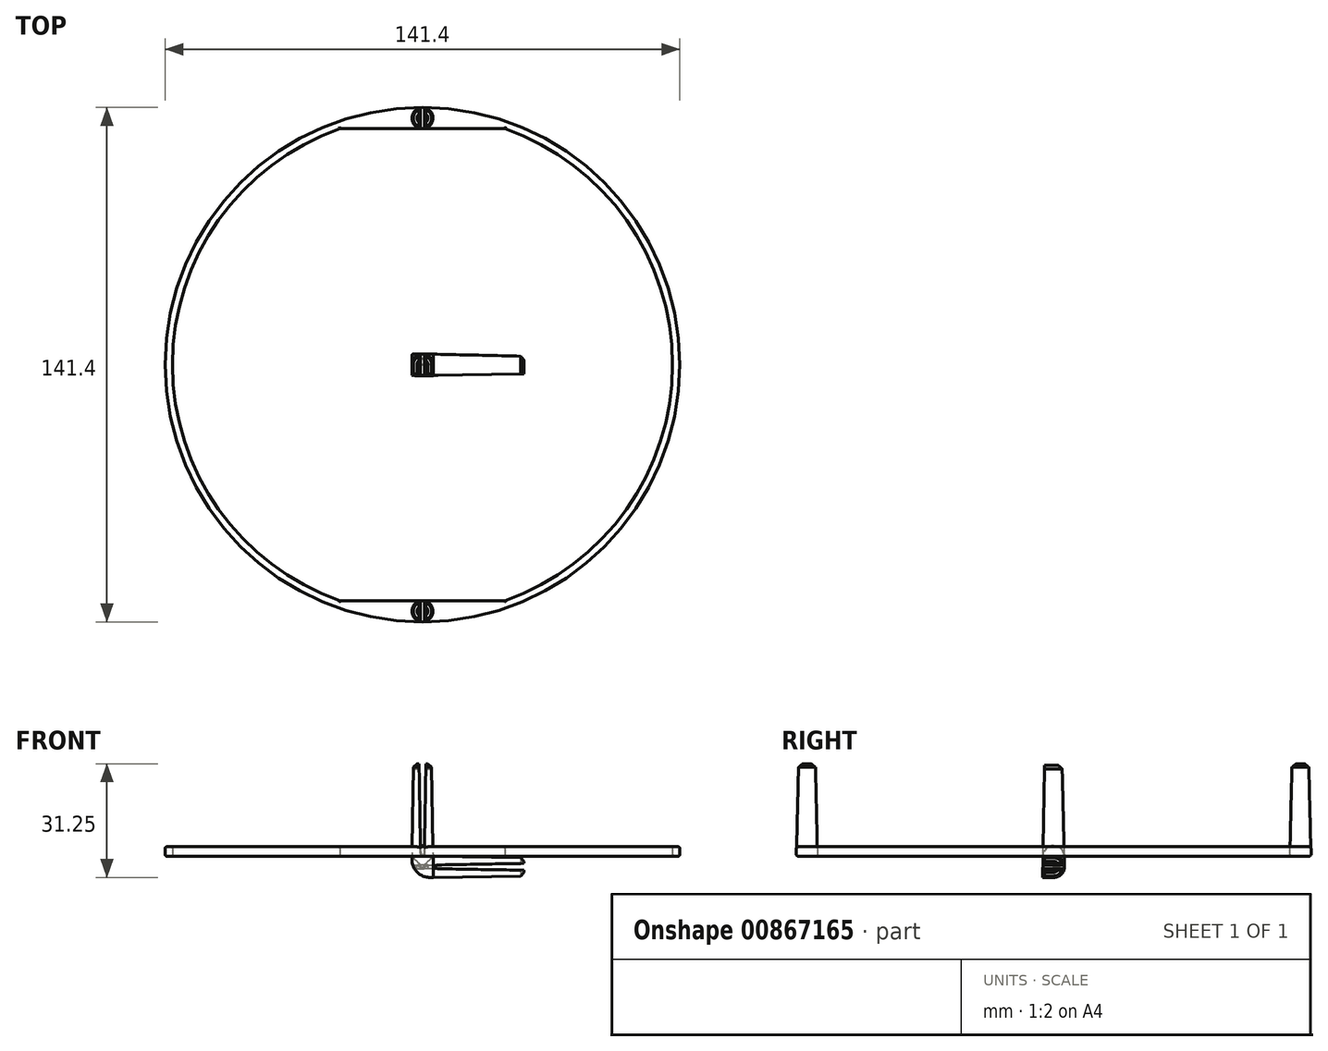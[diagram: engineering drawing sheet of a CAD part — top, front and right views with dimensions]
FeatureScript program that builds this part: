
annotation { "Feature Type Name" : "Feature", "Feature Type Description" : "" }
export const myFeature = defineFeature(function(context is Context, id is Id, definition is map)
    precondition{}
    {
        {
            assignVariable(context, id + "F0", {"name" : "discHeight", "anyValue" : 2.58});
        }
        {
            var Q0;
            Q0=qCreatedBy(makeId("Top.planeOp"),FACE);
            var sketch = newSketch(context, id + "F1", { "sketchPlane" : qUnion([Q0])});
            skCircle(sketch, "E0", {"center": v(0, 0) * mm, "radius": 70.7 * mm});
            skCircle(sketch, "E1", {"center": v(0, 0) * mm, "radius": 68.7 * mm});
            skLineSegment(sketch, "E2", {"start": v(0, -64.84) * mm, "end": v(0, -70.7) * mm, "construction": true});
            skLineSegment(sketch, "E3", {"start": v(0, -70.7) * mm, "end": v(0, -67.77) * mm, "construction": true});
            skCircle(sketch, "E4", {"center": v(0, -67.77) * mm, "radius": 2.92 * mm});
            skLineSegment(sketch, "E5", {"start": v(0, 0) * mm, "end": v(-70.7, 0) * mm, "construction": true});
            skLineSegment(sketch, "E6", {"start": v(0, -64.84) * mm, "end": v(22.67, -64.84) * mm});
            skLineSegment(sketch, "E7.MirrorCS", {"start": v(0, -64.84) * mm, "end": v(-22.67, -64.84) * mm});
            skLineSegment(sketch, "E8.MirrorCS", {"start": v(0, 64.84) * mm, "end": v(-22.67, 64.84) * mm});
            skLineSegment(sketch, "E9.MirrorCS", {"start": v(0, 64.84) * mm, "end": v(22.67, 64.84) * mm});
            skLineSegment(sketch, "E10.0", {"start": v(0.5, -70.7) * mm, "end": v(0.5, -67.77) * mm});
            skLineSegment(sketch, "E11.MirrorCS", {"start": v(-0.5, -70.7) * mm, "end": v(-0.5, -67.77) * mm});
            skLineSegment(sketch, "E12", {"start": v(0, -67.77) * mm, "end": v(-2.92, -67.77) * mm, "construction": true});
            skLineSegment(sketch, "E13.MirrorCS", {"start": v(-0.5, -64.84) * mm, "end": v(-0.5, -67.77) * mm});
            skLineSegment(sketch, "E14.MirrorCS", {"start": v(0.5, -64.84) * mm, "end": v(0.5, -67.77) * mm});
            skSolve(sketch);
        }
        {
            var Q0;
            {var subQ0=sQuery(id+"F1.wireOp",EDGE,"E0");Q0=makeQuery(id+"F1.imprint","IMPRINT",FACE,{"disambiguationData":[TD([[makeQuery(id+"F1.imprint","IMPRINT",EDGE,{"derivedFrom":subQ0}),1.0]])]});}
            var Q1;
            {var subQ0=sQuery(id+"F1.wireOp",EDGE,"E4");var subQ1=sQuery(id+"F1.wireOp",EDGE,"E1");var subQ2=makeQuery(id+"F1.imprint","INTERSECT",VERTEX,{"disambiguationData":[OD(0.0)],"derivedFrom":[subQ1,subQ0]});Q1=makeQuery(id+"F1.imprint","IMPRINT",FACE,{"disambiguationData":[TD([[makeQuery(id+"F1.imprint","IMPRINT",EDGE,{"disambiguationData":[TD([[subQ2,-1.0]])],"derivedFrom":subQ1}),-1.0]])]});}
            var Q2;
            {var subQ0=sQuery(id+"F1.wireOp",EDGE,"E7.MirrorCS");Q2=makeQuery(id+"F1.imprint","IMPRINT",FACE,{"disambiguationData":[TD([[makeQuery(id+"F1.imprint","IMPRINT",EDGE,{"derivedFrom":subQ0}),1.0]])]});}
            var Q3;
            {var subQ0=sQuery(id+"F1.wireOp",EDGE,"E6");Q3=makeQuery(id+"F1.imprint","IMPRINT",FACE,{"disambiguationData":[TD([[makeQuery(id+"F1.imprint","IMPRINT",EDGE,{"derivedFrom":subQ0}),-1.0]])]});}
            var Q4;
            {var subQ0=sQuery(id+"F1.wireOp",EDGE,"E8.MirrorCS");Q4=makeQuery(id+"F1.imprint","IMPRINT",FACE,{"disambiguationData":[TD([[makeQuery(id+"F1.imprint","IMPRINT",EDGE,{"derivedFrom":subQ0}),-1.0]])]});}
            var Q5;
            {var subQ0=sQuery(id+"F1.wireOp",EDGE,"E4");var subQ1=sQuery(id+"F1.wireOp",EDGE,"E1");var subQ2=makeQuery(id+"F1.imprint","INTERSECT",VERTEX,{"disambiguationData":[OD(0.0)],"derivedFrom":[subQ1,subQ0]});Q5=makeQuery(id+"F1.imprint","IMPRINT",FACE,{"disambiguationData":[TD([[makeQuery(id+"F1.imprint","IMPRINT",EDGE,{"disambiguationData":[TD([[subQ2,-1.0]])],"derivedFrom":subQ1}),1.0]])]});}
            var Q6;
            {var subQ0=sQuery(id+"F1.wireOp",EDGE,"E6");var subQ1=sQuery(id+"F1.wireOp",EDGE,"E1");var subQ2=makeQuery(id+"F1.imprint","INTERSECT",VERTEX,{"derivedFrom":[subQ1,subQ0]});Q6=makeQuery(id+"F1.imprint","IMPRINT",FACE,{"disambiguationData":[TD([[makeQuery(id+"F1.imprint","IMPRINT",EDGE,{"disambiguationData":[TD([[subQ2,1.0]])],"derivedFrom":subQ1}),1.0]])]});}
            var Q7;
            {var subQ0=sQuery(id+"F1.wireOp",EDGE,"E7.MirrorCS");var subQ1=sQuery(id+"F1.wireOp",EDGE,"E1");var subQ2=makeQuery(id+"F1.imprint","INTERSECT",VERTEX,{"derivedFrom":[subQ1,subQ0]});Q7=makeQuery(id+"F1.imprint","IMPRINT",FACE,{"disambiguationData":[TD([[makeQuery(id+"F1.imprint","IMPRINT",EDGE,{"disambiguationData":[TD([[subQ2,-1.0]])],"derivedFrom":subQ1}),1.0]])]});}
            var Q8;
            {var subQ0=sQuery(id+"F1.wireOp",EDGE,"E10.0");var subQ1=sQuery(id+"F1.wireOp",EDGE,"E1");var subQ2=makeQuery(id+"F1.imprint","INTERSECT",VERTEX,{"derivedFrom":[subQ1,subQ0]});Q8=makeQuery(id+"F1.imprint","IMPRINT",FACE,{"disambiguationData":[TD([[makeQuery(id+"F1.imprint","IMPRINT",EDGE,{"disambiguationData":[TD([[subQ2,-1.0]])],"derivedFrom":subQ1}),1.0]])]});}
            var Q9;
            {var subQ0=sQuery(id+"F1.wireOp",EDGE,"E10.0");var subQ1=sQuery(id+"F1.wireOp",EDGE,"E1");var subQ2=makeQuery(id+"F1.imprint","INTERSECT",VERTEX,{"derivedFrom":[subQ1,subQ0]});Q9=makeQuery(id+"F1.imprint","IMPRINT",FACE,{"disambiguationData":[TD([[makeQuery(id+"F1.imprint","IMPRINT",EDGE,{"disambiguationData":[TD([[subQ2,-1.0]])],"derivedFrom":subQ1}),-1.0]])]});}
            var Q10;
            {var subQ1=sQuery(id+"F1.wireOp",EDGE,"E1");var subQ6=sQuery(id+"F1.wireOp",EDGE,"E11.MirrorCS");var subQ8=makeQuery(id+"F1.imprint","INTERSECT",VERTEX,{"derivedFrom":[subQ1,subQ6]});Q10=makeQuery(id+"F1.imprint","IMPRINT",FACE,{"disambiguationData":[TD([[makeQuery(id+"F1.imprint","IMPRINT",EDGE,{"disambiguationData":[TD([[subQ8,-1.0]])],"derivedFrom":subQ1}),-1.0]])]});}
            var Q11;
            {var subQ6=sQuery(id+"F1.wireOp",EDGE,"E1");var subQ10=sQuery(id+"F1.wireOp",EDGE,"E11.MirrorCS");var subQ11=makeQuery(id+"F1.imprint","INTERSECT",VERTEX,{"derivedFrom":[subQ6,subQ10]});Q11=makeQuery(id+"F1.imprint","IMPRINT",FACE,{"disambiguationData":[TD([[makeQuery(id+"F1.imprint","IMPRINT",EDGE,{"disambiguationData":[TD([[subQ11,-1.0]])],"derivedFrom":subQ6}),1.0]])]});}
            var Q12;
            {var subQ6=sQuery(id+"F1.wireOp",EDGE,"E11.MirrorCS");var subQ9=sQuery(id+"F1.wireOp",EDGE,"E0");var subQ12=makeQuery(id+"F1.imprint","INTERSECT",VERTEX,{"derivedFrom":[subQ9,subQ6]});Q12=makeQuery(id+"F1.imprint","IMPRINT",FACE,{"disambiguationData":[TD([[makeQuery(id+"F1.imprint","IMPRINT",EDGE,{"disambiguationData":[TD([[subQ12,1.0]])],"derivedFrom":subQ9}),1.0]])]});}
            extrude(context, id + "F2", {"entities" : qUnion([Q0, Q1, Q2, Q3, Q4, Q5, Q6, Q7, Q8, Q9, Q10, Q11, Q12]), "depth" : (getVariable(context, 'discHeight')) * mm, "offsetDistance" : 25 * mm});
        }
        {
            assignVariable(context, id + "F3", {"name" : "mountHeight", "anyValue" : 25.4});
        }
        {
            var Q0;
            {var subQ0=sQuery(id+"F1.wireOp",EDGE,"E4");var subQ1=sQuery(id+"F1.wireOp",EDGE,"E1");var subQ2=makeQuery(id+"F1.imprint","INTERSECT",VERTEX,{"disambiguationData":[OD(0.0)],"derivedFrom":[subQ1,subQ0]});Q0=makeQuery(id+"F1.imprint","IMPRINT",FACE,{"disambiguationData":[TD([[makeQuery(id+"F1.imprint","IMPRINT",EDGE,{"disambiguationData":[TD([[subQ2,-1.0]])],"derivedFrom":subQ1}),1.0]])]});}
            var Q1;
            {var subQ0=sQuery(id+"F1.wireOp",EDGE,"E4");var subQ1=sQuery(id+"F1.wireOp",EDGE,"E1");var subQ2=makeQuery(id+"F1.imprint","INTERSECT",VERTEX,{"disambiguationData":[OD(0.0)],"derivedFrom":[subQ1,subQ0]});Q1=makeQuery(id+"F1.imprint","IMPRINT",FACE,{"disambiguationData":[TD([[makeQuery(id+"F1.imprint","IMPRINT",EDGE,{"disambiguationData":[TD([[subQ2,-1.0]])],"derivedFrom":subQ1}),-1.0]])]});}
            var Q2;
            {var subQ0=sQuery(id+"F1.wireOp",EDGE,"E10.0");var subQ1=sQuery(id+"F1.wireOp",EDGE,"E1");var subQ2=makeQuery(id+"F1.imprint","INTERSECT",VERTEX,{"derivedFrom":[subQ1,subQ0]});Q2=makeQuery(id+"F1.imprint","IMPRINT",FACE,{"disambiguationData":[TD([[makeQuery(id+"F1.imprint","IMPRINT",EDGE,{"disambiguationData":[TD([[subQ2,-1.0]])],"derivedFrom":subQ1}),1.0]])]});}
            var Q3;
            {var subQ0=sQuery(id+"F1.wireOp",EDGE,"E10.0");var subQ1=sQuery(id+"F1.wireOp",EDGE,"E1");var subQ2=makeQuery(id+"F1.imprint","INTERSECT",VERTEX,{"derivedFrom":[subQ1,subQ0]});Q3=makeQuery(id+"F1.imprint","IMPRINT",FACE,{"disambiguationData":[TD([[makeQuery(id+"F1.imprint","IMPRINT",EDGE,{"disambiguationData":[TD([[subQ2,-1.0]])],"derivedFrom":subQ1}),-1.0]])]});}
            extrude(context, id + "F4", {"entities" : qUnion([Q0, Q1, Q2, Q3]), "depth" : (getVariable(context, 'mountHeight')) * mm, "offsetDistance" : 25 * mm, "hasDraft" : true, "draftAngle" : 1 * degree, "draftPullDirection" : true});
        }
        {
            var Q0;
            Q0=makeQuery(id+"F4.opExtrude","SWEPT_BODY",BODY,{"disambiguationData":[OSD([sQuery(id+"F1.wireOp",EDGE,"E4")])]});
            var Q1;
            Q1=qCreatedBy(makeId("Front.planeOp"),FACE);
            mirror(context, id + "F5", {"operationType" : NewBodyOperationType.ADD, "entities" : qUnion([Q0]), "mirrorPlane" : qUnion([Q1])});
        }
        {
            var Q0;
            Q0=makeQuery(id+"F5.opPattern","COPY",EDGE,{"derivedFrom":makeQuery(id+"F4.opExtrude","CAP_EDGE",EDGE,{"disambiguationData":[OSD([sQuery(id+"F1.wireOp",EDGE,"E4")])],"isStart":false}),"instanceName":"1"});
            var Q1;
            Q1=makeQuery(id+"F4.opExtrude","CAP_EDGE",EDGE,{"disambiguationData":[OSD([sQuery(id+"F1.wireOp",EDGE,"E4")])],"isStart":false});
            chamfer(context, id + "F6", {"entities" : qUnion([Q0, Q1]), "width" : 1 * mm, "tangentPropagation" : true});
        }
        {
            var Q0;
            Q0=makeQuery(id+"F5.boolean.opBoolean","SPLIT",EDGE,{"disambiguationData":[OD(0.0)],"derivedFrom":makeQuery(id+"F2.opExtrude","CAP_EDGE",EDGE,{"disambiguationData":[OSD([sQuery(id+"F1.wireOp",EDGE,"E1")])],"isStart":false})});
            var Q1;
            Q1=makeQuery(id+"F2.opExtrude","CAP_EDGE",EDGE,{"disambiguationData":[OSD([sQuery(id+"F1.wireOp",EDGE,"E0")])],"isStart":false});
            var Q2;
            Q2=makeQuery(id+"F5.boolean.opBoolean","SPLIT",EDGE,{"disambiguationData":[OD(1.0)],"derivedFrom":makeQuery(id+"F2.opExtrude","CAP_EDGE",EDGE,{"disambiguationData":[OSD([sQuery(id+"F1.wireOp",EDGE,"E1")])],"isStart":true})});
            var Q3;
            Q3=makeQuery(id+"F2.opExtrude","CAP_EDGE",EDGE,{"disambiguationData":[OSD([sQuery(id+"F1.wireOp",EDGE,"E0")])],"isStart":true});
            var Q4;
            Q4=makeQuery(id+"F5.opPattern","COPY",EDGE,{"derivedFrom":makeQuery(id+"F4.opExtrude","CAP_EDGE",EDGE,{"disambiguationData":[OSD([sQuery(id+"F1.wireOp",EDGE,"E4")])],"isStart":true}),"instanceName":"1"});
            var Q5;
            Q5=makeQuery(id+"F5.boolean.opBoolean","SPLIT",EDGE,{"disambiguationData":[OD(1.0)],"derivedFrom":makeQuery(id+"F2.opExtrude","CAP_EDGE",EDGE,{"disambiguationData":[OSD([sQuery(id+"F1.wireOp",EDGE,"E1")])],"isStart":false})});
            var Q6;
            Q6=makeQuery(id+"F4.opExtrude","CAP_EDGE",EDGE,{"disambiguationData":[OSD([sQuery(id+"F1.wireOp",EDGE,"E4")])],"isStart":true});
            var Q7;
            Q7=makeQuery(id+"F5.boolean.opBoolean","SPLIT",EDGE,{"disambiguationData":[OD(0.0)],"derivedFrom":makeQuery(id+"F2.opExtrude","CAP_EDGE",EDGE,{"disambiguationData":[OSD([sQuery(id+"F1.wireOp",EDGE,"E1")])],"isStart":true})});
            var Q8;
            Q8=makeQuery(id+"F2.opExtrude","CAP_EDGE",EDGE,{"disambiguationData":[OSD([sQuery(id+"F1.wireOp",EDGE,"E6"),sQuery(id+"F1.wireOp",EDGE,"E7.MirrorCS")])],"isStart":false});
            var Q9;
            Q9=makeQuery(id+"F2.opExtrude","CAP_EDGE",EDGE,{"disambiguationData":[OSD([sQuery(id+"F1.wireOp",EDGE,"E6"),sQuery(id+"F1.wireOp",EDGE,"E7.MirrorCS")])],"isStart":true});
            var Q10;
            Q10=makeQuery(id+"F2.opExtrude","CAP_EDGE",EDGE,{"disambiguationData":[OSD([sQuery(id+"F1.wireOp",EDGE,"E8.MirrorCS"),sQuery(id+"F1.wireOp",EDGE,"E9.MirrorCS")])],"isStart":false});
            var Q11;
            Q11=makeQuery(id+"F2.opExtrude","CAP_EDGE",EDGE,{"disambiguationData":[OSD([sQuery(id+"F1.wireOp",EDGE,"E8.MirrorCS"),sQuery(id+"F1.wireOp",EDGE,"E9.MirrorCS")])],"isStart":true});
            fillet(context, id + "F7", {"entities" : qUnion([Q0, Q1, Q2, Q3, Q4, Q5, Q6, Q7, Q8, Q9, Q10, Q11]), "radius" : 0.5 * mm, "tangentPropagation" : true, "allowEdgeOverflow" : false});
        }
        {
            var Q0;
            Q0=qCreatedBy(makeId("Top.planeOp"),FACE);
            var sketch = newSketch(context, id + "F8", { "sketchPlane" : qUnion([Q0])});
            skCircle(sketch, "E15", {"center": v(0, 0) * mm, "radius": 2.93 * mm});
            skLineSegment(sketch, "E16", {"start": v(0, 2.93) * mm, "end": v(0, -2.93) * mm});
            skLineSegment(sketch, "E17.0", {"start": v(0.5, 2.88) * mm, "end": v(0.5, -2.88) * mm});
            skLineSegment(sketch, "E18.MirrorCS", {"start": v(-0.5, 2.88) * mm, "end": v(-0.5, -2.88) * mm});
            skPoint(sketch, "E19.orphan", {"position": v(0.5, 2.92) * mm});
            skPoint(sketch, "E20.orphan", {"position": v(-0.5, 2.92) * mm});
            skPoint(sketch, "E21.orphan", {"position": v(0.5, -2.93) * mm});
            skPoint(sketch, "E22.orphan", {"position": v(-0.5, -2.93) * mm});
            skLineSegment(sketch, "E23.top", {"start": v(-2.93, -2.93) * mm, "end": v(2.93, -2.93) * mm});
            skLineSegment(sketch, "E23.left", {"start": v(-2.93, 0) * mm, "end": v(-2.93, -2.93) * mm});
            skLineSegment(sketch, "E23.right", {"start": v(2.93, 0) * mm, "end": v(2.93, -2.93) * mm});
            skSolve(sketch);
        }
        {
            var Q0;
            {var subQ0=sQuery(id+"F8.wireOp",EDGE,"E16");Q0=makeQuery(id+"F8.imprint","IMPRINT",FACE,{"disambiguationData":[TD([[makeQuery(id+"F8.imprint","IMPRINT",EDGE,{"derivedFrom":subQ0}),1.0]])]});}
            var Q1;
            {var subQ0=sQuery(id+"F8.wireOp",EDGE,"E17.0");Q1=makeQuery(id+"F8.imprint","IMPRINT",FACE,{"disambiguationData":[TD([[makeQuery(id+"F8.imprint","IMPRINT",EDGE,{"derivedFrom":subQ0}),1.0]])]});}
            var Q2;
            Q2=sQuery(id+"F8.wireOp",EDGE,"E16");
            revolve(context, id + "F9", {"surfaceOperationType" : NewSurfaceOperationType.NEW, "entities" : qUnion([Q0, Q1]), "axis" : qUnion([Q2]), "revolveType" : RevolveType.FULL});
        }
        {
            var Q0;
            {var subQ0=sQuery(id+"F8.wireOp",EDGE,"E17.0");Q0=makeQuery(id+"F8.imprint","IMPRINT",FACE,{"disambiguationData":[TD([[makeQuery(id+"F8.imprint","IMPRINT",EDGE,{"derivedFrom":subQ0}),1.0]])]});}
            var Q1;
            {var subQ0=sQuery(id+"F8.wireOp",EDGE,"E18.MirrorCS");Q1=makeQuery(id+"F8.imprint","IMPRINT",FACE,{"disambiguationData":[TD([[makeQuery(id+"F8.imprint","IMPRINT",EDGE,{"derivedFrom":subQ0}),-1.0]])]});}
            var Q2;
            {var subQ2=sQuery(id+"F8.wireOp",EDGE,"E23.left");Q2=makeQuery(id+"F8.imprint","IMPRINT",FACE,{"disambiguationData":[TD([[makeQuery(id+"F8.imprint","IMPRINT",EDGE,{"derivedFrom":subQ2}),1.0]])]});}
            var Q3;
            {var subQ4=sQuery(id+"F8.wireOp",EDGE,"E23.right");Q3=makeQuery(id+"F8.imprint","IMPRINT",FACE,{"disambiguationData":[TD([[makeQuery(id+"F8.imprint","IMPRINT",EDGE,{"derivedFrom":subQ4}),-1.0]])]});}
            extrude(context, id + "F10", {"entities" : qUnion([Q0, Q1, Q2, Q3]), "depth" : 25 * mm, "offsetDistance" : 25 * mm, "hasDraft" : true, "draftAngle" : 1 * degree, "draftPullDirection" : true});
        }
        {
            var Q0;
            {var subQ0=sQuery(id+"F8.wireOp",EDGE,"E18.MirrorCS");var subQ1=sQuery(id+"F8.wireOp",EDGE,"E15");Q0=makeQuery(id+"F10.opExtrude","CAP_EDGE",EDGE,{"disambiguationData":[OSD([subQ1]),TDD([makeQuery(id+"F8.imprint","IMPRINT",EDGE,{"disambiguationData":[TD([[makeQuery(id+"F8.imprint","INTERSECT",VERTEX,{"disambiguationData":[OD(0.0)],"derivedFrom":[subQ1,subQ0]}),-1.0]])],"derivedFrom":subQ1})])],"isStart":false});}
            var Q1;
            {var subQ0=sQuery(id+"F8.wireOp",EDGE,"E17.0");var subQ1=sQuery(id+"F8.wireOp",EDGE,"E15");Q1=makeQuery(id+"F10.opExtrude","CAP_EDGE",EDGE,{"disambiguationData":[OSD([subQ1]),TDD([makeQuery(id+"F8.imprint","IMPRINT",EDGE,{"disambiguationData":[TD([[makeQuery(id+"F8.imprint","INTERSECT",VERTEX,{"disambiguationData":[OD(0.0)],"derivedFrom":[subQ1,subQ0]}),1.0]])],"derivedFrom":subQ1})])],"isStart":false});}
            chamfer(context, id + "F11", {"entities" : qUnion([Q0, Q1]), "width" : 1 * mm, "tangentPropagation" : true});
        }
        {
            var Q0;
            Q0=makeQuery(id+"F10.opExtrude","SWEPT_BODY",BODY,{"disambiguationData":[OSD([sQuery(id+"F8.wireOp",EDGE,"E15"),sQuery(id+"F8.wireOp",EDGE,"E18.MirrorCS")])]});
            var Q1;
            Q1=makeQuery(id+"F10.opExtrude","SWEPT_BODY",BODY,{"disambiguationData":[OSD([sQuery(id+"F8.wireOp",EDGE,"E15"),sQuery(id+"F8.wireOp",EDGE,"E17.0")])]});
            var Q2;
            Q2=sQuery(id+"F8.wireOp",EDGE,"E23.left");
            transform(context, id + "F12", {"entities" : qUnion([Q0, Q1]), "transformType" : TransformType.ROTATION, "transformAxis" : qUnion([Q2]), "angle" : 90 * degree, "oppositeDirection" : true, "makeCopy" : true});
        }
        {
            var Q0;
            Q0=makeQuery(id+"F12.opPattern","COPY",BODY,{"derivedFrom":makeQuery(id+"F10.opExtrude","SWEPT_BODY",BODY,{"disambiguationData":[OSD([sQuery(id+"F8.wireOp",EDGE,"E15"),sQuery(id+"F8.wireOp",EDGE,"E18.MirrorCS"),sQuery(id+"F8.wireOp",EDGE,"E23.top"),sQuery(id+"F8.wireOp",EDGE,"E23.left")])]}),"instanceName":"1"});
            var Q1;
            Q1=makeQuery(id+"F12.opPattern","COPY",BODY,{"derivedFrom":makeQuery(id+"F10.opExtrude","SWEPT_BODY",BODY,{"disambiguationData":[OSD([sQuery(id+"F8.wireOp",EDGE,"E15"),sQuery(id+"F8.wireOp",EDGE,"E17.0"),sQuery(id+"F8.wireOp",EDGE,"E23.top"),sQuery(id+"F8.wireOp",EDGE,"E23.right")])]}),"instanceName":"1"});
            var Q2;
            Q2=sQuery(id+"F8.wireOp",EDGE,"E23.top");
            transform(context, id + "F13", {"entities" : qUnion([Q0, Q1]), "transformType" : TransformType.TRANSLATION_ENTITY, "oppositeDirectionEntity" : false, "transformLine" : qUnion([Q2]), "makeCopy" : false});
        }
        {
            var Q0;
            Q0=qCreatedBy(makeId("Front.planeOp"),FACE);
            var sketch = newSketch(context, id + "F14", { "sketchPlane" : qUnion([Q0])});
            skPoint(sketch, "E24.0", {"position": v(2.93, -5.85) * mm});
            skPoint(sketch, "E25.0", {"position": v(-2.93, 0) * mm});
            skLineSegment(sketch, "E26.0", {"start": v(2.93, 0) * mm, "end": v(2.93, -2.93) * mm});
            skLineSegment(sketch, "E26.1", {"start": v(2.93, -2.93) * mm, "end": v(2.93, -5.85) * mm});
            skLineSegment(sketch, "E26.2", {"start": v(-2.93, 0) * mm, "end": v(2.93, 0) * mm});
            skLineSegment(sketch, "E27.bottom", {"start": v(2.93, -5.85) * mm, "end": v(-2.93, -5.85) * mm});
            skLineSegment(sketch, "E27.top", {"start": v(2.93, 0) * mm, "end": v(-2.93, 0) * mm});
            skLineSegment(sketch, "E27.left", {"start": v(2.93, -5.85) * mm, "end": v(2.93, 0) * mm});
            skLineSegment(sketch, "E27.right", {"start": v(-2.93, -5.85) * mm, "end": v(-2.93, 0) * mm});
            skSolve(sketch);
        }
        {
            var Q0;
            Q0 = qSketchRegion(id + "F14", true);
            var Q1;
            {var subQ0=sQuery(id+"F8.wireOp",EDGE,"E23.top");Q1=makeQuery(id+"F10.opExtrude","SWEPT_FACE",FACE,{"disambiguationData":[OSD([subQ0]),TDD([makeQuery(id+"F8.imprint","IMPRINT",EDGE,{"disambiguationData":[TD([[makeQuery(id+"F8.imprint","INTERSECT",VERTEX,{"derivedFrom":[subQ0,sQuery(id+"F8.wireOp",EDGE,"E23.left")]}),-1.0]])],"derivedFrom":subQ0})])]});}
            extrude(context, id + "F15", {"entities" : qUnion([Q0]), "endBound" : BoundingType.UP_TO_SURFACE, "depth" : 25 * mm, "endBoundEntityFace" : qUnion([Q1]), "offsetDistance" : 25 * mm});
        }
        {
            var Q0;
            Q0=makeQuery(id+"F12.opPattern","COPY",FACE,{"derivedFrom":makeQuery(id+"F10.opExtrude","CAP_FACE",FACE,{"disambiguationData":[OSD([sQuery(id+"F8.wireOp",EDGE,"E15"),sQuery(id+"F8.wireOp",EDGE,"E17.0"),sQuery(id+"F8.wireOp",EDGE,"E23.top"),sQuery(id+"F8.wireOp",EDGE,"E23.right")])],"isStart":true}),"instanceName":"1"});
            var Q1;
            Q1=makeQuery(id+"F12.opPattern","COPY",FACE,{"derivedFrom":makeQuery(id+"F10.opExtrude","CAP_FACE",FACE,{"disambiguationData":[OSD([sQuery(id+"F8.wireOp",EDGE,"E15"),sQuery(id+"F8.wireOp",EDGE,"E18.MirrorCS"),sQuery(id+"F8.wireOp",EDGE,"E23.top"),sQuery(id+"F8.wireOp",EDGE,"E23.left")])],"isStart":true}),"instanceName":"1"});
            var Q2;
            Q2=makeQuery(id+"F15.opExtrude","SWEPT_FACE",FACE,{"disambiguationData":[OSD([sQuery(id+"F14.wireOp",EDGE,"E27.right")])]});
            extrude(context, id + "F16", {"entities" : qUnion([Q0, Q1]), "operationType" : NewBodyOperationType.ADD, "endBound" : BoundingType.UP_TO_SURFACE, "depth" : 25 * mm, "endBoundEntityFace" : qUnion([Q2]), "offsetDistance" : 25 * mm});
        }
        {
            var Q0;
            {var subQ0=sQuery(id+"F8.wireOp",EDGE,"E18.MirrorCS");Q0=makeQuery(id+"F8.imprint","IMPRINT",FACE,{"disambiguationData":[TD([[makeQuery(id+"F8.imprint","IMPRINT",EDGE,{"derivedFrom":subQ0}),-1.0]])]});}
            var Q1;
            {var subQ0=sQuery(id+"F8.wireOp",EDGE,"E17.0");Q1=makeQuery(id+"F8.imprint","IMPRINT",FACE,{"disambiguationData":[TD([[makeQuery(id+"F8.imprint","IMPRINT",EDGE,{"derivedFrom":subQ0}),1.0]])]});}
            var Q2;
            Q2=makeQuery(id+"F16.opExtrude","SWEPT_FACE",FACE,{"disambiguationData":[OSD([sQuery(id+"F8.wireOp",EDGE,"E18.MirrorCS")])]});
            extrude(context, id + "F17", {"entities" : qUnion([Q0, Q1]), "operationType" : NewBodyOperationType.ADD, "endBound" : BoundingType.UP_TO_SURFACE, "oppositeDirection" : true, "depth" : 25 * mm, "endBoundEntityFace" : qUnion([Q2]), "offsetDistance" : 25 * mm});
        }
        {
            var Q0;
            {var subQ0=sQuery(id+"F8.wireOp",EDGE,"E16");Q0=makeQuery(id+"F8.imprint","IMPRINT",FACE,{"disambiguationData":[TD([[makeQuery(id+"F8.imprint","IMPRINT",EDGE,{"derivedFrom":subQ0}),1.0]])]});}
            var Q1;
            {var subQ0=sQuery(id+"F8.wireOp",EDGE,"E16");Q1=makeQuery(id+"F8.imprint","IMPRINT",FACE,{"disambiguationData":[TD([[makeQuery(id+"F8.imprint","IMPRINT",EDGE,{"derivedFrom":subQ0}),-1.0]])]});}
            var Q2;
            Q2=makeQuery(id+"F16.opExtrude","SWEPT_FACE",FACE,{"disambiguationData":[OSD([sQuery(id+"F8.wireOp",EDGE,"E18.MirrorCS")])]});
            extrude(context, id + "F18", {"entities" : qUnion([Q0, Q1]), "operationType" : NewBodyOperationType.ADD, "endBound" : BoundingType.UP_TO_SURFACE, "oppositeDirection" : true, "depth" : 25 * mm, "endBoundEntityFace" : qUnion([Q2]), "offsetDistance" : 25 * mm});
        }
        {
            var Q0;
            {var subQ0=sQuery(id+"F8.wireOp",EDGE,"E18.MirrorCS");Q0=makeQuery(id+"F18.boolean.opBoolean","MERGE",FACE,{"derivedFrom":[makeQuery(id+"F16.opExtrude","SWEPT_FACE",FACE,{"disambiguationData":[OSD([subQ0])]}),makeQuery(id+"F18.opExtrude","CAP_FACE",FACE,{"disambiguationData":[OSD([subQ0])],"isStart":false})]});}
            var Q1;
            Q1=makeQuery(id+"F16.opExtrude","SWEPT_FACE",FACE,{"disambiguationData":[OSD([sQuery(id+"F8.wireOp",EDGE,"E17.0")])]});
            extrude(context, id + "F19", {"entities" : qUnion([Q0]), "operationType" : NewBodyOperationType.ADD, "endBound" : BoundingType.UP_TO_SURFACE, "depth" : 25 * mm, "endBoundEntityFace" : qUnion([Q1]), "offsetDistance" : 25 * mm});
        }
        {
            var Q0;
            Q0=makeQuery(id+"F15.opExtrude","SWEPT_EDGE",EDGE,{"disambiguationData":[OSD([sQuery(id+"F14.wireOp",EDGE,"E27.bottom"),sQuery(id+"F14.wireOp",EDGE,"E27.right")])]});
            fillet(context, id + "F20", {"entities" : qUnion([Q0]), "radius" : 5 * mm, "tangentPropagation" : true, "allowEdgeOverflow" : false});
        }
    });
